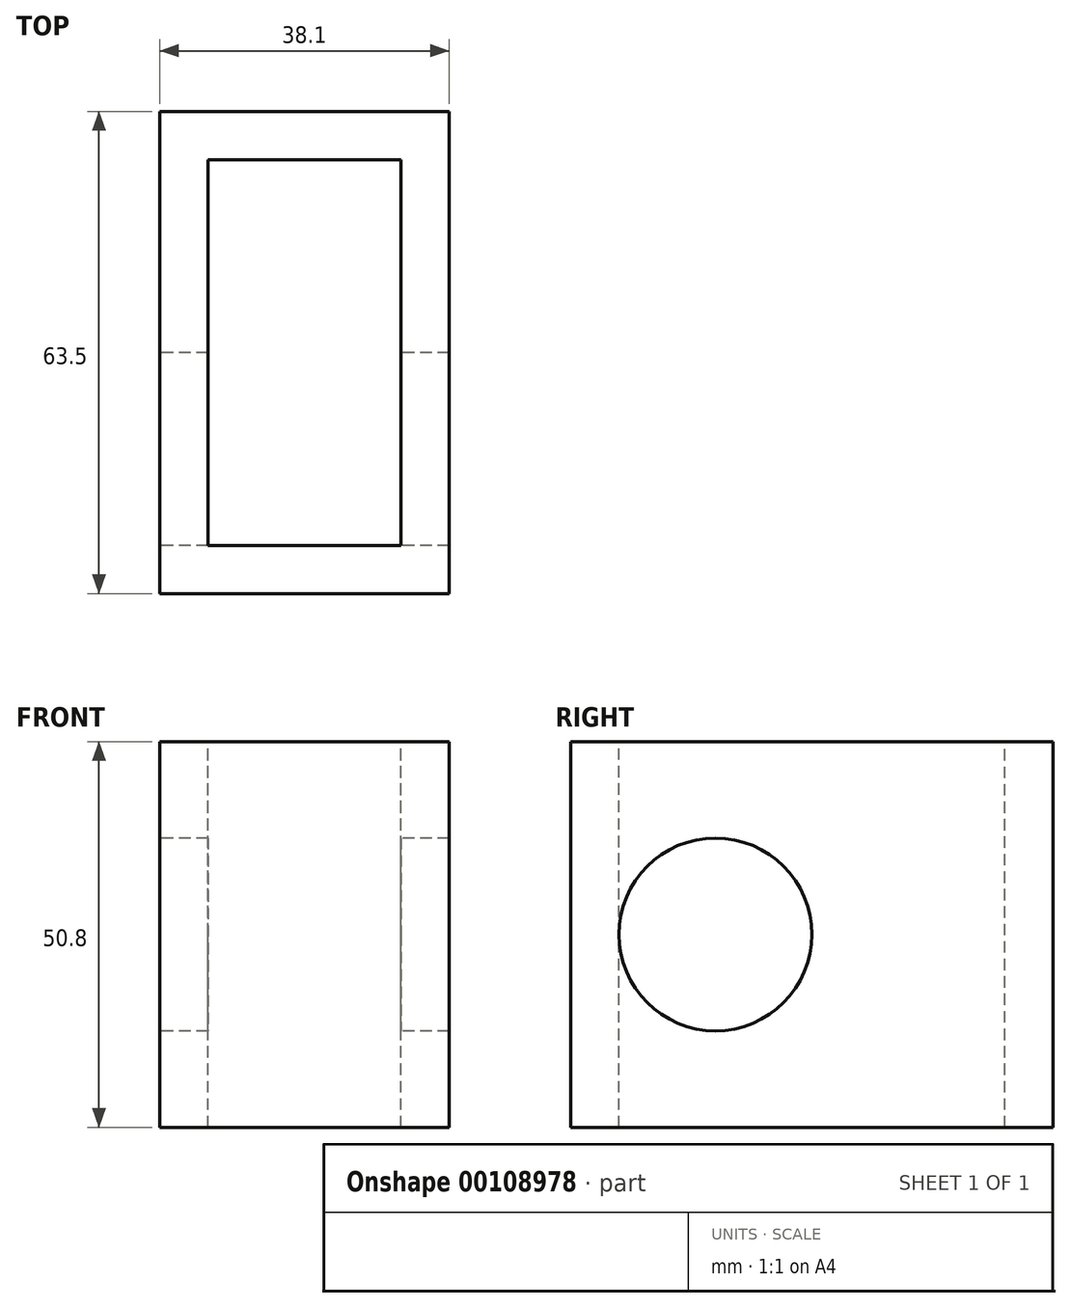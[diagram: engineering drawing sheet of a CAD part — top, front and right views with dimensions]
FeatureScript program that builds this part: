
annotation { "Feature Type Name" : "Feature", "Feature Type Description" : "" }
export const myFeature = defineFeature(function(context is Context, id is Id, definition is map)
    precondition{}
    {
        {
            var Q0;
            Q0=qCreatedBy(makeId("Right.planeOp"),FACE);
            var sketch = newSketch(context, id + "F0", { "sketchPlane" : qUnion([Q0])});
            skLineSegment(sketch, "E0.bottom", {"start": v(31.75, 25.4) * mm, "end": v(-31.75, 25.4) * mm});
            skLineSegment(sketch, "E0.top", {"start": v(31.75, -25.4) * mm, "end": v(-31.75, -25.4) * mm});
            skLineSegment(sketch, "E0.left", {"start": v(31.75, 25.4) * mm, "end": v(31.75, -25.4) * mm});
            skLineSegment(sketch, "E0.right", {"start": v(-31.75, 25.4) * mm, "end": v(-31.75, -25.4) * mm});
            skPoint(sketch, "E0.middle", {"position": v(0, 0) * mm});
            skPoint(sketch, "E1.endSnap0", {"position": v(-31.75, 0) * mm});
            skCircle(sketch, "E2", {"center": v(-12.7, 0) * mm, "radius": 12.7 * mm});
            skSolve(sketch);
        }
        {
            var Q0;
            Q0=makeQuery(id+"F0.imprint","IMPRINT",FACE,{"disambiguationData":[TD([[makeQuery(id+"F0.imprint","IMPRINT",EDGE,{"derivedFrom":sQuery(id+"F0.wireOp",EDGE,"E0.bottom")}),1.0]])]});
            extrude(context, id + "F1", {"entities" : qUnion([Q0]), "depth" : 38.1 * mm});
        }
        {
            var Q0;
            Q0=makeQuery(id+"F1.opExtrude","SWEPT_FACE",FACE,{"disambiguationData":[OSD([sQuery(id+"F0.wireOp",EDGE,"E0.bottom")])]});
            var sketch = newSketch(context, id + "F2", { "sketchPlane" : qUnion([Q0])});
            skLineSegment(sketch, "E3", {"start": v(6.35, 25.4) * mm, "end": v(6.35, -25.4) * mm});
            skLineSegment(sketch, "E4", {"start": v(6.35, 25.4) * mm, "end": v(31.75, 25.4) * mm});
            skLineSegment(sketch, "E5", {"start": v(31.75, -25.4) * mm, "end": v(31.75, 25.4) * mm});
            skLineSegment(sketch, "E6", {"start": v(31.75, -25.4) * mm, "end": v(6.35, -25.4) * mm});
            skPoint(sketch, "E7.orphan", {"position": v(33.18, 25.4) * mm});
            skSolve(sketch);
        }
        {
            var Q0;
            Q0=makeQuery(id+"F2.imprint","IMPRINT",FACE,{"disambiguationData":[TD([[makeQuery(id+"F2.imprint","IMPRINT",EDGE,{"derivedFrom":sQuery(id+"F2.wireOp",EDGE,"E3")}),1.0]])]});
            extrude(context, id + "F3", {"entities" : qUnion([Q0]), "operationType" : NewBodyOperationType.REMOVE, "endBound" : BoundingType.THROUGH_ALL, "oppositeDirection" : true, "depth" : 25.4 * mm});
        }
    });
